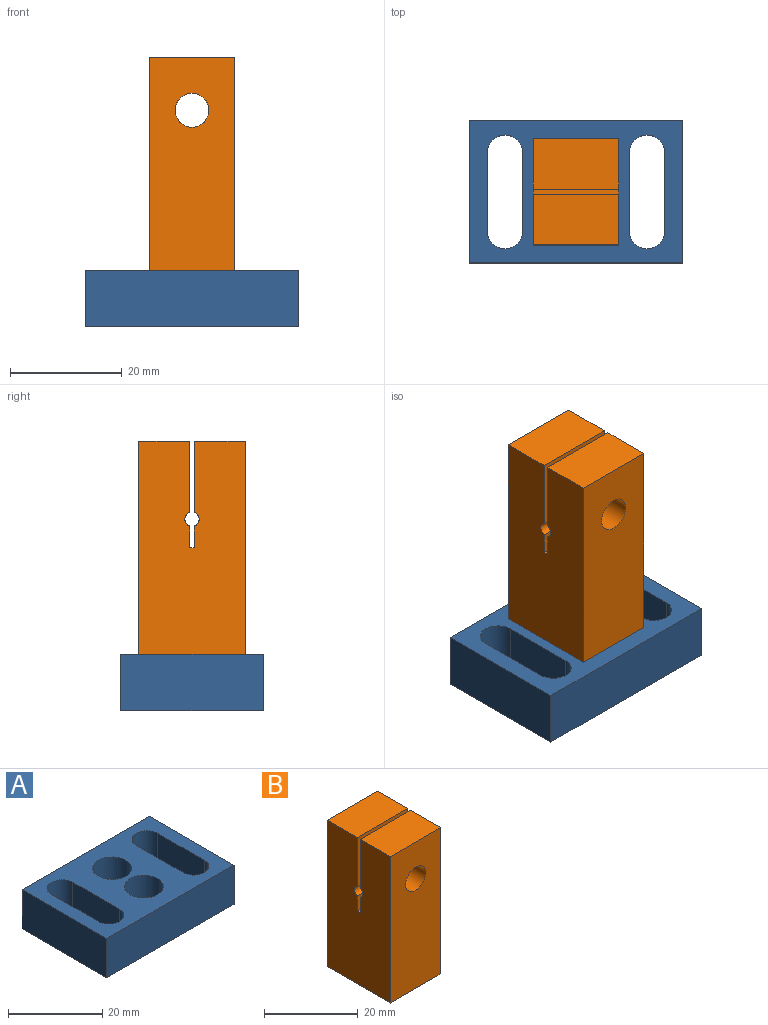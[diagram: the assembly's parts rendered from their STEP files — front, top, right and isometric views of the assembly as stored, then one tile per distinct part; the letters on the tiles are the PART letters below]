
ASSEMBLY  parts=2 mates=1
PART A: 20 faces, bbox 38.1x25.4x10.2 mm
  f0: plane 38.1x10.16mm, normal (0,-1,0), area 387.1mm2, adj f1,f11,f12,f13
  f1: plane 25.4x10.16mm, normal (1,0,0), area 258.1mm2, adj f0,f2,f12,f13
  f2: plane 38.1x10.16mm, normal (0,1,0), area 387.1mm2, adj f1,f11,f12,f13
  f3: cylinder r=3.17mm len=10.16mm, axis (0,0,1), area 101.3mm2, adj f4,f9,f12,f13
  f4: plane 13.97x10.16mm, normal (-1,0,0), area 141.9mm2, adj f3,f5,f12,f13
  f5: cylinder r=3.17mm len=10.16mm, axis (0,0,1), area 101.3mm2, adj f4,f9,f12,f13
  f6: cylinder r=3.17mm len=10.16mm, axis (0,0,1), area 101.3mm2, adj f7,f10,f12,f13
  f7: plane 13.97x10.16mm, normal (1,0,0), area 141.9mm2, adj f6,f8,f12,f13
  f8: cylinder r=3.17mm len=10.16mm, axis (0,0,1), area 101.3mm2, adj f7,f10,f12,f13
  f9: plane 13.97x10.16mm, normal (1,0,0), area 141.9mm2, adj f3,f5,f12,f13
  f10: plane 13.97x10.16mm, normal (-1,0,0), area 141.9mm2, adj f6,f8,f12,f13
  f11: plane 25.4x10.16mm, normal (-1,0,0), area 258.1mm2, adj f0,f2,f12,f13
  f12: plane 38.1x25.4mm, normal (0,0,-1), area 686.4mm2, adj f0,f1,f2,f3,f4,f5,f6,f7
  f13: plane 38.1x25.4mm, normal (0,0,1), area 619.9mm2, adj f0,f1,f2,f3,f4,f5,f6,f7
  f14: cylinder r=2.54mm len=5.08mm, axis (0,0,1), area 40.5mm2, adj f12,f15
  f15: plane 8.26x8.26mm, normal (0,0,1), area 33.3mm2, adj f14,f16
  f16: cylinder r=4.13mm len=8.26mm, axis (0,0,1), area 197.6mm2, adj f13,f15
  f17: cylinder r=2.54mm len=5.08mm, axis (0,0,1), area 40.5mm2, adj f12,f18
  f18: plane 8.26x8.26mm, normal (0,0,1), area 33.3mm2, adj f17,f19
  f19: cylinder r=4.13mm len=8.26mm, axis (0,0,1), area 197.6mm2, adj f13,f18
PART B: 20 faces, bbox 15.2x19.1x38.1 mm
  f0: plane 15.24x12.78mm, normal (0,1,0), area 166.1mm2, adj f1,f11,f12,f13,f19
  f1: plane 15.24x9.08mm, normal (0,0,1), area 138.4mm2, adj f0,f2,f12,f13
  f2: plane 38.1x15.24mm, normal (0,-1,0), area 551.9mm2, adj f1,f3,f12,f13,f19
  f3: plane 19.05x15.24mm, normal (0,0,-1), area 249.8mm2, adj f2,f4,f12,f13,f14,f16
  f4: plane 38.1x15.24mm, normal (0,1,0), area 551.9mm2, adj f3,f5,f12,f13,f18
  f5: plane 15.24x9.08mm, normal (0,0,1), area 138.4mm2, adj f4,f6,f12,f13
  f6: plane 15.24x12.78mm, normal (0,-1,0), area 166.1mm2, adj f5,f7,f12,f13,f18
  f7: cylinder r=1.27mm len=15.24mm, axis (1,0,0), area 47mm2, adj f6,f8,f12,f13
  f8: plane 15.24x3.89mm, normal (0,-1,0), area 59.3mm2, adj f7,f9,f12,f13
  f9: plane 15.24x0.89mm, normal (0,0,1), area 13.5mm2, adj f8,f10,f12,f13
  f10: plane 15.24x3.89mm, normal (0,1,0), area 59.3mm2, adj f9,f11,f12,f13
  f11: cylinder r=1.27mm len=15.24mm, axis (1,0,0), area 47mm2, adj f0,f10,f12,f13
  f12: plane 38.1x19.05mm, normal (-1,0,0), area 706mm2, adj f0,f1,f2,f3,f4,f5,f6,f7
  f13: plane 38.1x19.05mm, normal (1,0,0), area 706mm2, adj f0,f1,f2,f3,f4,f5,f6,f7
  f14: cylinder r=2.54mm len=10.16mm, axis (0,0,-1), area 162.1mm2, adj f3,f15
  f15: plane 5.08x5.08mm, normal (0,0,-1), area 20.3mm2, adj f14
  f16: cylinder r=2.54mm len=10.16mm, axis (0,0,-1), area 162.1mm2, adj f3,f17
  f17: plane 5.08x5.08mm, normal (0,0,-1), area 20.3mm2, adj f16
  f18: cylinder r=3.02mm len=9.08mm, axis (0,1,0), area 172.5mm2, adj f4,f6
  f19: cylinder r=3.02mm len=9.08mm, axis (0,1,0), area 172.5mm2, adj f0,f2
PLACE A rot(axis=(1,0,0),180deg) t=(-3.1,-22.03,2.39)mm
PLACE B t=(-14.53,-25.21,12.55)mm
MATE cylindrical B.f16 <-> A.f17  axis (0,0,-1) through (-22.15,-39.5,12.55)mm
